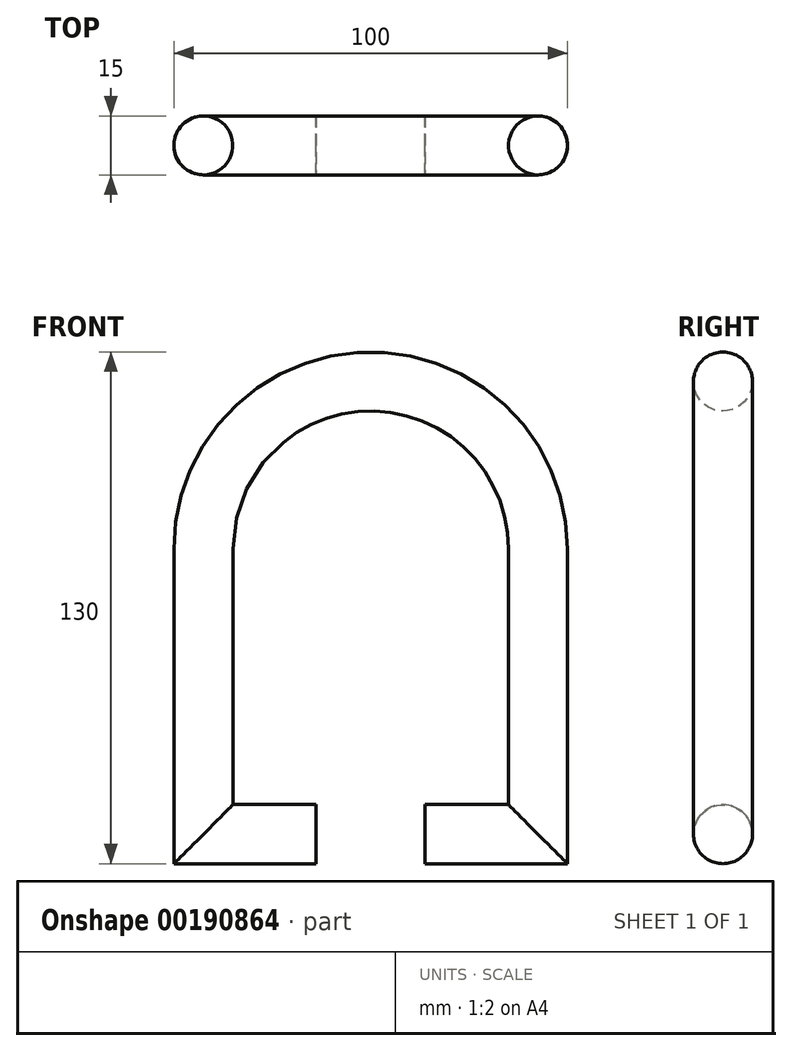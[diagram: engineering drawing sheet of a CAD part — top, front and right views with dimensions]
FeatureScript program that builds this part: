
annotation { "Feature Type Name" : "Feature", "Feature Type Description" : "" }
export const myFeature = defineFeature(function(context is Context, id is Id, definition is map)
    precondition{}
    {
        {
            var Q0;
            Q0=qCreatedBy(makeId("Front.planeOp"),FACE);
            var sketch = newSketch(context, id + "F0", { "sketchPlane" : qUnion([Q0])});
            skLineSegment(sketch, "E0", {"start": v(-13.83, 0) * mm, "end": v(-42.5, 0) * mm});
            skLineSegment(sketch, "E1", {"start": v(-42.5, 0) * mm, "end": v(-42.5, 72.5) * mm});
            skArc(sketch, "E2", {"start": v(0, 115) * mm, "mid": v(-30.05, 102.55) * mm, "end": v(-42.5, 72.5) * mm});
            skArc(sketch, "E3.MirrorCS", {"start": v(0, 115) * mm, "mid": v(30.05, 102.55) * mm, "end": v(42.5, 72.5) * mm});
            skLineSegment(sketch, "E4.MirrorCS", {"start": v(42.5, 0) * mm, "end": v(42.5, 72.5) * mm});
            skLineSegment(sketch, "E5.MirrorCS", {"start": v(13.83, 0) * mm, "end": v(42.5, 0) * mm});
            skSolve(sketch);
        }
        {
            var Q0;
            Q0=sQuery(id+"F0.wireOp",VERTEX,"E0.start");
            var Q1;
            Q1=qCreatedBy(makeId("Right.planeOp"),FACE);
            cPlane(context, id + "F1", {"entities" : qUnion([Q0, Q1]), "cplaneType" : CPlaneType.PLANE_POINT, "offset" : 25 * mm, "width" : 150 * mm, "height" : 150 * mm});
        }
        {
            var Q0;
            Q0=qCreatedBy(id+"F1.planeOp",FACE);
            var sketch = newSketch(context, id + "F2", { "sketchPlane" : qUnion([Q0])});
            skCircle(sketch, "E6", {"center": v(0, 0) * mm, "radius": 7.5 * mm});
            skSolve(sketch);
        }
        {
            var Q0;
            Q0=makeQuery(id+"F2.imprint","IMPRINT",FACE,{"disambiguationData":[TD([[makeQuery(id+"F2.imprint","IMPRINT",EDGE,{"derivedFrom":sQuery(id+"F2.wireOp",EDGE,"E6")}),1.0]])]});
            var Q1;
            Q1=sQuery(id+"F0.wireOp",EDGE,"E2");
            var Q2;
            Q2=sQuery(id+"F0.wireOp",EDGE,"E1");
            var Q3;
            Q3=sQuery(id+"F0.wireOp",EDGE,"E0");
            var Q4;
            Q4=sQuery(id+"F0.wireOp",EDGE,"E3.MirrorCS");
            var Q5;
            Q5=sQuery(id+"F0.wireOp",EDGE,"E4.MirrorCS");
            var Q6;
            Q6=sQuery(id+"F0.wireOp",EDGE,"E5.MirrorCS");
            sweep(context, id + "F3", {"profiles" : qUnion([Q0]), "path" : qUnion([Q1, Q2, Q3, Q4, Q5, Q6])});
        }
    });
